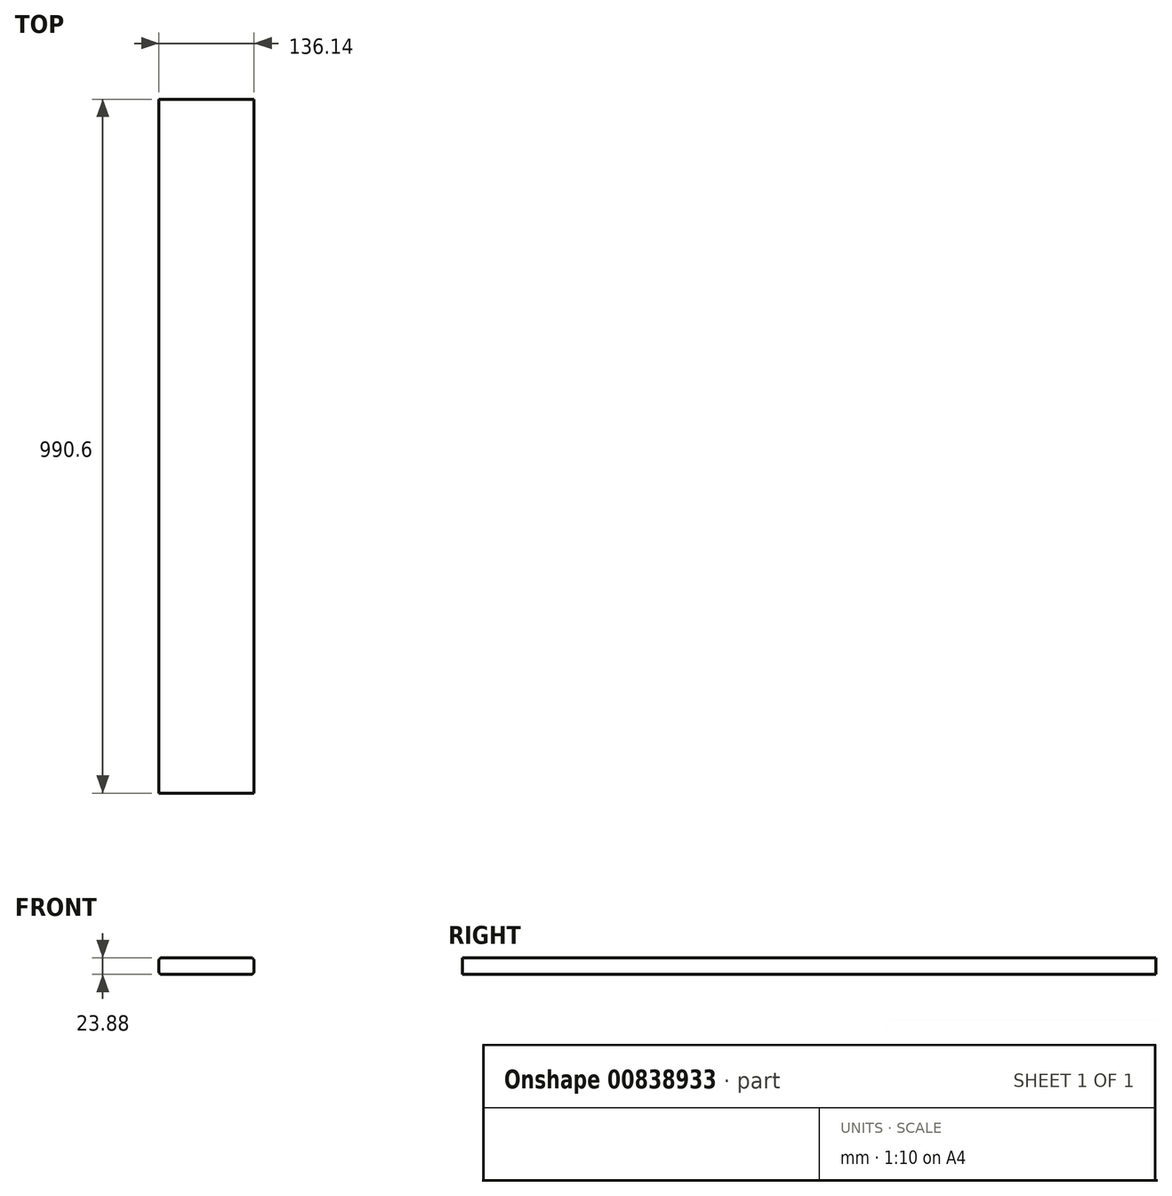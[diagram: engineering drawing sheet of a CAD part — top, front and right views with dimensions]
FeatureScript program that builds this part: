
annotation { "Feature Type Name" : "Feature", "Feature Type Description" : "" }
export const myFeature = defineFeature(function(context is Context, id is Id, definition is map)
    precondition{}
    {
        {
            var Q0;
            Q0=qCreatedBy(makeId("Front.planeOp"),FACE);
            var sketch = newSketch(context, id + "F0", { "sketchPlane" : qUnion([Q0])});
            skLineSegment(sketch, "E0.bottom", {"start": v(-63.25, 11.94) * mm, "end": v(63.25, 11.94) * mm});
            skLineSegment(sketch, "E0.top", {"start": v(-63.25, -11.94) * mm, "end": v(63.25, -11.94) * mm});
            skLineSegment(sketch, "E0.left", {"start": v(-68.07, 7.11) * mm, "end": v(-68.07, -7.11) * mm});
            skLineSegment(sketch, "E0.right", {"start": v(68.07, 7.11) * mm, "end": v(68.07, -7.11) * mm});
            skPoint(sketch, "E0.middle", {"position": v(0, 0) * mm});
            skPoint(sketch, "E1.visualSharp", {"position": v(-68.07, 11.94) * mm});
            skArc(sketch, "E1.filletArc", {"start": v(-63.25, 11.94) * mm, "mid": v(-66.66, 10.52) * mm, "end": v(-68.07, 7.11) * mm});
            skPoint(sketch, "E2.visualSharp", {"position": v(68.07, 11.94) * mm});
            skArc(sketch, "E2.filletArc", {"start": v(68.07, 7.11) * mm, "mid": v(66.66, 10.52) * mm, "end": v(63.25, 11.94) * mm});
            skPoint(sketch, "E3.visualSharp", {"position": v(68.07, -11.94) * mm});
            skArc(sketch, "E3.filletArc", {"start": v(63.25, -11.94) * mm, "mid": v(66.66, -10.52) * mm, "end": v(68.07, -7.11) * mm});
            skPoint(sketch, "E4.visualSharp", {"position": v(-68.07, -11.94) * mm});
            skArc(sketch, "E4.filletArc", {"start": v(-68.07, -7.11) * mm, "mid": v(-66.66, -10.52) * mm, "end": v(-63.25, -11.94) * mm});
            skSolve(sketch);
        }
        {
            var Q0;
            Q0=makeQuery(id+"F0.imprint","IMPRINT",FACE,{"disambiguationData":[TD([[makeQuery(id+"F0.imprint","IMPRINT",EDGE,{"derivedFrom":sQuery(id+"F0.wireOp",EDGE,"E0.bottom")}),-1.0]])]});
            extrude(context, id + "F1", {"entities" : qUnion([Q0]), "endBound" : BoundingType.SYMMETRIC, "depth" : 990.6 * mm, "offsetDistance" : 25.4 * mm});
        }
    });
